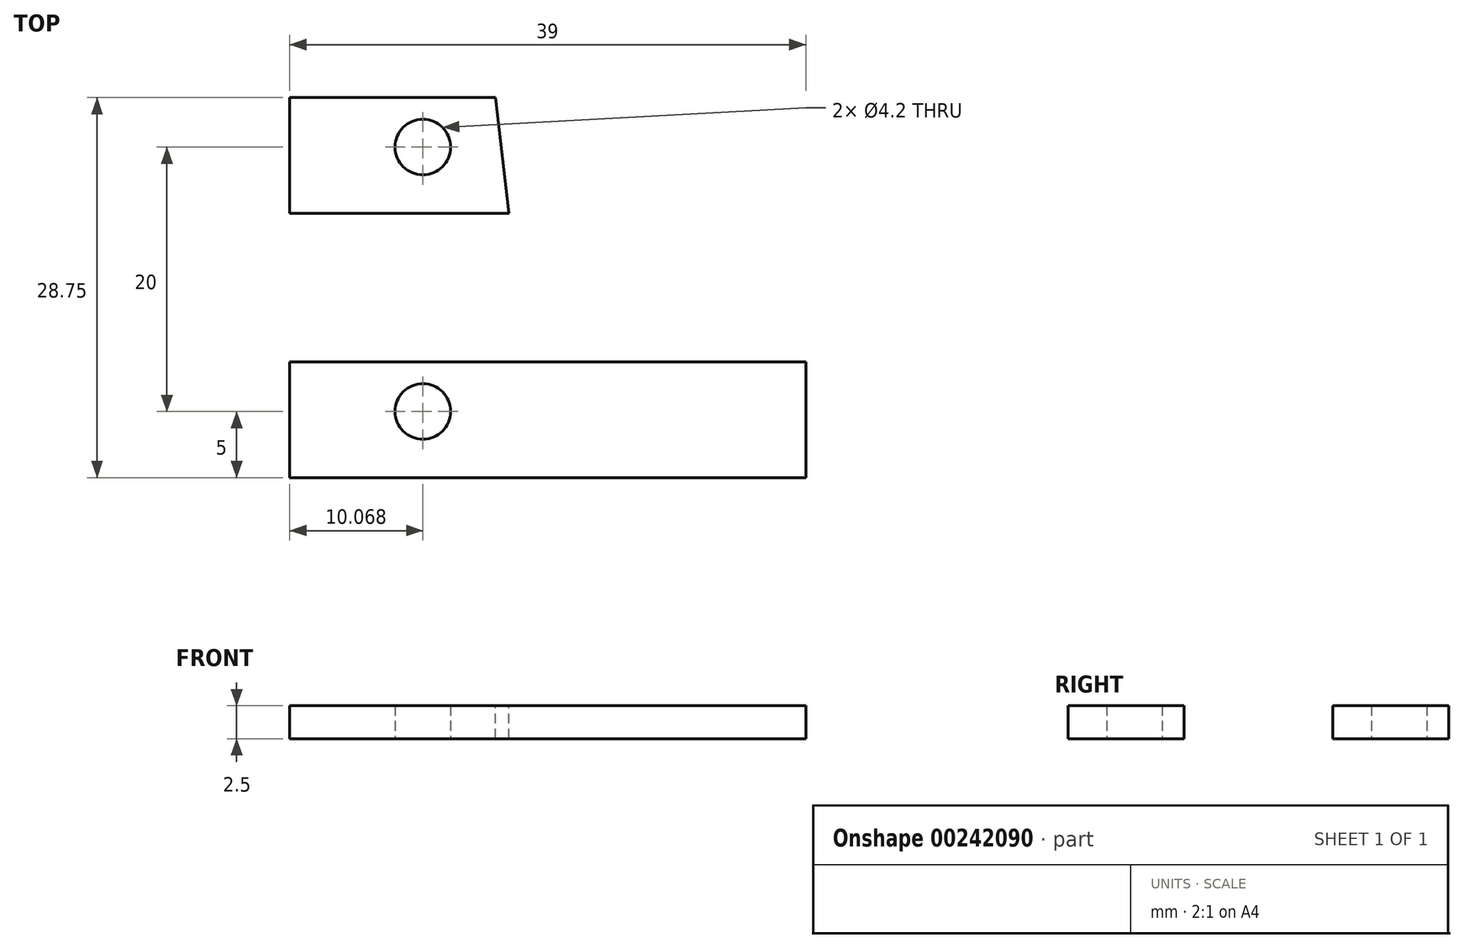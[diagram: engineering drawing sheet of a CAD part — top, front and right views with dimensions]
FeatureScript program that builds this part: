
annotation { "Feature Type Name" : "Feature", "Feature Type Description" : "" }
export const myFeature = defineFeature(function(context is Context, id is Id, definition is map)
    precondition{}
    {
        {
            var Q0;
            Q0=qCreatedBy(makeId("Top.planeOp"),FACE);
            var sketch = newSketch(context, id + "F0", { "sketchPlane" : qUnion([Q0])});
            skLineSegment(sketch, "E0.bottom", {"start": v(-4.64, 10) * mm, "end": v(14.36, 10) * mm});
            skLineSegment(sketch, "E0.top", {"start": v(-4.64, 0) * mm, "end": v(14.36, 0) * mm});
            skLineSegment(sketch, "E0.left", {"start": v(-4.64, 10) * mm, "end": v(-4.64, 0) * mm});
            skLineSegment(sketch, "E0.right", {"start": v(14.36, 10) * mm, "end": v(14.36, 0) * mm});
            skLineSegment(sketch, "E1", {"start": v(5.43, 0) * mm, "end": v(5.43, 10) * mm, "construction": true});
            skCircle(sketch, "E2", {"center": v(5.43, 5) * mm, "radius": 2.1 * mm});
            skLineSegment(sketch, "E3.bottom", {"start": v(14.36, 10) * mm, "end": v(34.36, 10) * mm});
            skLineSegment(sketch, "E3.top", {"start": v(14.36, 0) * mm, "end": v(34.36, 0) * mm});
            skLineSegment(sketch, "E3.right", {"start": v(34.36, 10) * mm, "end": v(34.36, 0) * mm});
            skSolve(sketch);
        }
        {
            var Q0;
            Q0 = qSketchRegion(id + "F0", true);
            var Q1;
            Q1=makeQuery(id+"F0.imprint","IMPRINT",FACE,{"disambiguationData":[TD([[makeQuery(id+"F0.imprint","IMPRINT",EDGE,{"derivedFrom":sQuery(id+"F0.wireOp",EDGE,"E0.bottom")}),-1.0]])]});
            extrude(context, id + "F1", {"entities" : qUnion([Q0, Q1]), "depth" : 2.5 * mm});
        }
        {
            var Q0;
            Q0=makeQuery(id+"F1.opExtrude","CAP_FACE",FACE,{"disambiguationData":[OSD([sQuery(id+"F0.wireOp",EDGE,"E0.bottom"),sQuery(id+"F0.wireOp",EDGE,"E0.top"),sQuery(id+"F0.wireOp",EDGE,"E0.left"),sQuery(id+"F0.wireOp",EDGE,"E2"),sQuery(id+"F0.wireOp",EDGE,"E3.bottom"),sQuery(id+"F0.wireOp",EDGE,"E3.top"),sQuery(id+"F0.wireOp",EDGE,"E3.right")])],"isStart":false});
            var sketch = newSketch(context, id + "F2", { "sketchPlane" : qUnion([Q0])});
            skCircle(sketch, "E4", {"center": v(-4.64, 10) * mm, "radius": 1.25 * mm, "construction": true});
            skCircle(sketch, "E5", {"center": v(34.36, 10) * mm, "radius": 1.25 * mm, "construction": true});
            skLineSegment(sketch, "E6", {"start": v(-4.64, 8.75) * mm, "end": v(34.36, 8.75) * mm});
            skSolve(sketch);
        }
        {
            var Q0;
            {var subQ0=sQuery(id+"F2.wireOp",EDGE,"E6");Q0=makeQuery(id+"F2.imprint","IMPRINT",FACE,{"disambiguationData":[TD([[makeQuery(id+"F2.imprint","IMPRINT",EDGE,{"derivedFrom":subQ0}),1.0]])]});}
            extrude(context, id + "F3", {"entities" : qUnion([Q0]), "operationType" : NewBodyOperationType.REMOVE, "endBound" : BoundingType.THROUGH_ALL, "oppositeDirection" : true, "depth" : 25 * mm});
        }
        {
            var Q0;
            Q0=makeQuery(id+"F1.opExtrude","SWEPT_BODY",BODY,{"disambiguationData":[OSD([sQuery(id+"F0.wireOp",EDGE,"E0.bottom"),sQuery(id+"F0.wireOp",EDGE,"E0.top"),sQuery(id+"F0.wireOp",EDGE,"E0.left"),sQuery(id+"F0.wireOp",EDGE,"E2"),sQuery(id+"F0.wireOp",EDGE,"E3.bottom"),sQuery(id+"F0.wireOp",EDGE,"E3.top"),sQuery(id+"F0.wireOp",EDGE,"E3.right")])]});
            transform(context, id + "F4", {"entities" : qUnion([Q0]), "transformType" : TransformType.TRANSLATION_3D, "dx" : 0 * mm, "dy" : 20 * mm, "dz" : 0 * mm, "makeCopy" : true});
        }
        {
            var Q0;
            Q0=makeQuery(id+"F4.opPattern","COPY",FACE,{"derivedFrom":makeQuery(id+"F1.opExtrude","CAP_FACE",FACE,{"disambiguationData":[OSD([sQuery(id+"F0.wireOp",EDGE,"E0.bottom"),sQuery(id+"F0.wireOp",EDGE,"E0.top"),sQuery(id+"F0.wireOp",EDGE,"E0.left"),sQuery(id+"F0.wireOp",EDGE,"E2"),sQuery(id+"F0.wireOp",EDGE,"E3.bottom"),sQuery(id+"F0.wireOp",EDGE,"E3.top"),sQuery(id+"F0.wireOp",EDGE,"E3.right")])],"isStart":false}),"instanceName":"1"});
            var sketch = newSketch(context, id + "F5", { "sketchPlane" : qUnion([Q0])});
            skLineSegment(sketch, "E7", {"start": v(11.91, 20) * mm, "end": v(10.92, 28.75) * mm});
            skSolve(sketch);
        }
        {
            var Q0;
            {var subQ0=sQuery(id+"F5.wireOp",EDGE,"E7");Q0=makeQuery(id+"F5.imprint","IMPRINT",FACE,{"disambiguationData":[TD([[makeQuery(id+"F5.imprint","IMPRINT",EDGE,{"derivedFrom":subQ0}),-1.0]])]});}
            extrude(context, id + "F6", {"entities" : qUnion([Q0]), "operationType" : NewBodyOperationType.REMOVE, "endBound" : BoundingType.THROUGH_ALL, "oppositeDirection" : true, "depth" : 25 * mm});
        }
    });
